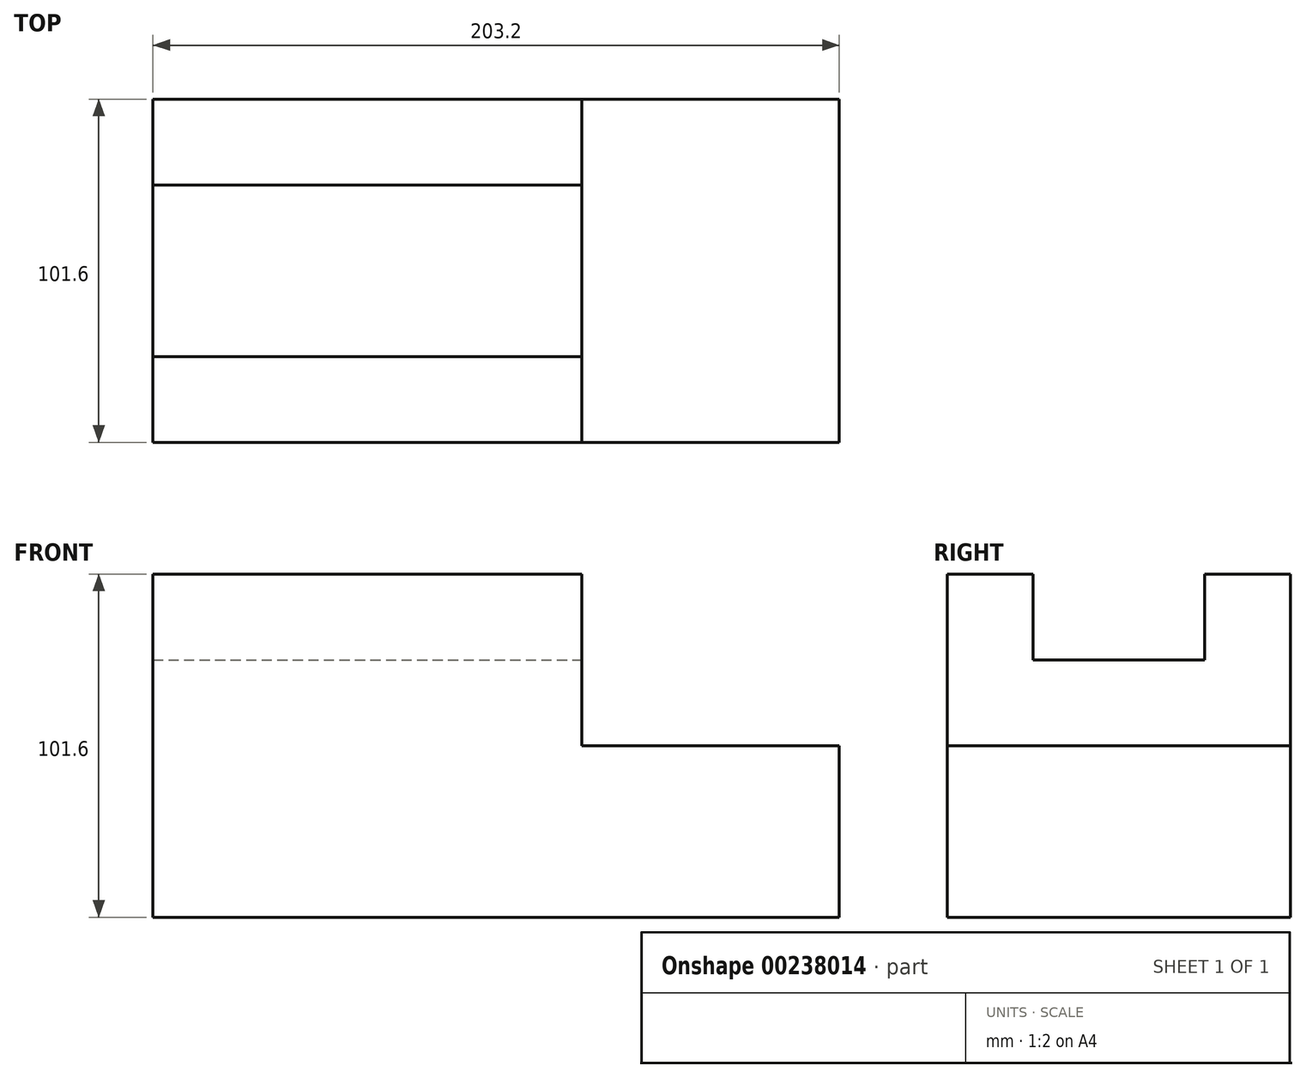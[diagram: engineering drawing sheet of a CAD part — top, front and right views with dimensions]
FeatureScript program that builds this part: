
annotation { "Feature Type Name" : "Feature", "Feature Type Description" : "" }
export const myFeature = defineFeature(function(context is Context, id is Id, definition is map)
    precondition{}
    {
        {
            var Q0;
            Q0=qCreatedBy(makeId("Front.planeOp"),FACE);
            var sketch = newSketch(context, id + "F0", { "sketchPlane" : qUnion([Q0])});
            skLineSegment(sketch, "E0.bottom", {"start": v(-97.26, 62.86) * mm, "end": v(105.94, 62.86) * mm});
            skLineSegment(sketch, "E0.top", {"start": v(-97.26, -38.74) * mm, "end": v(105.94, -38.74) * mm});
            skLineSegment(sketch, "E0.left", {"start": v(-97.26, 62.86) * mm, "end": v(-97.26, -38.74) * mm});
            skLineSegment(sketch, "E0.right", {"start": v(105.94, 62.86) * mm, "end": v(105.94, -38.74) * mm});
            skSolve(sketch);
        }
        {
            var Q0;
            Q0=makeQuery(id+"F0.imprint","IMPRINT",FACE,{"disambiguationData":[TD([[makeQuery(id+"F0.imprint","IMPRINT",EDGE,{"derivedFrom":sQuery(id+"F0.wireOp",EDGE,"E0.bottom")}),-1.0]])]});
            extrude(context, id + "F1", {"entities" : qUnion([Q0]), "depth" : 101.6 * mm});
        }
        {
            var Q0;
            Q0=makeQuery(id+"F1.opExtrude","SWEPT_FACE",FACE,{"disambiguationData":[OSD([sQuery(id+"F0.wireOp",EDGE,"E0.bottom")])]});
            var sketch = newSketch(context, id + "F2", { "sketchPlane" : qUnion([Q0])});
            skLineSegment(sketch, "E1.bottom", {"start": v(105.94, 0) * mm, "end": v(29.74, 0) * mm});
            skLineSegment(sketch, "E1.top", {"start": v(105.94, -101.6) * mm, "end": v(29.74, -101.6) * mm});
            skLineSegment(sketch, "E1.left", {"start": v(105.94, 0) * mm, "end": v(105.94, -101.6) * mm});
            skLineSegment(sketch, "E1.right", {"start": v(29.74, 0) * mm, "end": v(29.74, -101.6) * mm});
            skSolve(sketch);
        }
        {
            var Q0;
            Q0=makeQuery(id+"F2.imprint","IMPRINT",FACE,{"disambiguationData":[TD([[makeQuery(id+"F2.imprint","IMPRINT",EDGE,{"derivedFrom":sQuery(id+"F2.wireOp",EDGE,"E1.bottom")}),-1.0]])]});
            extrude(context, id + "F3", {"entities" : qUnion([Q0]), "operationType" : NewBodyOperationType.REMOVE, "oppositeDirection" : true, "depth" : 50.8 * mm});
        }
        {
            var Q0;
            Q0=makeQuery(id+"F1.opExtrude","SWEPT_FACE",FACE,{"disambiguationData":[OSD([sQuery(id+"F0.wireOp",EDGE,"E0.bottom")])]});
            var sketch = newSketch(context, id + "F4", { "sketchPlane" : qUnion([Q0])});
            skLineSegment(sketch, "E2.bottom", {"start": v(-97.26, -25.4) * mm, "end": v(29.74, -25.4) * mm});
            skLineSegment(sketch, "E2.top", {"start": v(-97.26, -76.2) * mm, "end": v(29.74, -76.2) * mm});
            skLineSegment(sketch, "E2.left", {"start": v(-97.26, -25.4) * mm, "end": v(-97.26, -76.2) * mm});
            skLineSegment(sketch, "E2.right", {"start": v(29.74, -25.4) * mm, "end": v(29.74, -76.2) * mm});
            skSolve(sketch);
        }
        {
            var Q0;
            Q0=makeQuery(id+"F4.imprint","IMPRINT",FACE,{"disambiguationData":[TD([[makeQuery(id+"F4.imprint","IMPRINT",EDGE,{"derivedFrom":sQuery(id+"F4.wireOp",EDGE,"E2.bottom")}),-1.0]])]});
            extrude(context, id + "F5", {"entities" : qUnion([Q0]), "operationType" : NewBodyOperationType.REMOVE, "oppositeDirection" : true, "depth" : 25.4 * mm});
        }
    });
